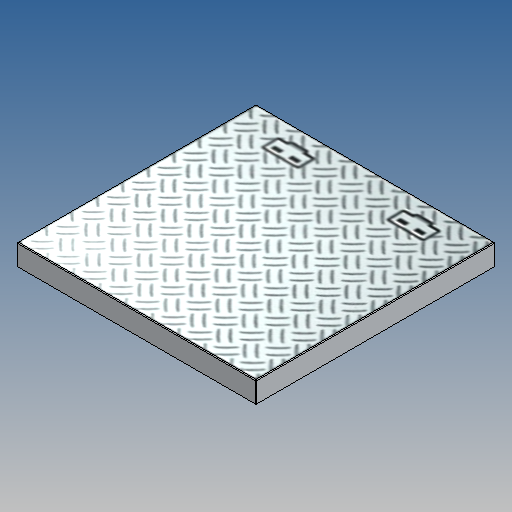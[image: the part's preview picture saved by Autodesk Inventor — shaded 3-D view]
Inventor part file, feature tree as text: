
AUTODESK INVENTOR PART (.ipt)
format: ipt  version: 2025 (Build 290162010, 162A)  size: 711,680 bytes
history: native  units: in
note: dims shown in document units (in); Inventor stores cm internally (conversion verified against a paired STEP export)
features: other x6, extrude x4, sketch x3, pattern_linear x1, fillet x1
ambient origin geometry x8: Origin, YZ Plane, XZ Plane, XY Plane, X Axis, Y Axis, Z Axis, Center Point
bodies: Solid1 (feature_tree)
feature tree (15):
  extrude  "Extrusion1"  Depth=1.2598in
  sketch  "Sketch3"  dims[d4=0.126in d5=0.0in d7=0.0591in d11=0.063in d12=0.0in]
  extrude  "Extrusion2"  Depth=0.063in TaperAngle=0.0deg
  extrude  "Extrusion7"  Depth=0.315in
  extrude  "Extrusion6"  Depth=0.315in
  pattern_linear  "Rectangular Pattern3"  Spacing1=0.6299in  [1 undecoded]
  fillet  "Fillet1"  Radius=0.126in
  other  "Work Axis1"
  other  "Work Axis2"
  other  "Work Axis3"
  other  "Work Axis4"
  other  "Aufkleber1"
  sketch  "Sketch2"  dims[d0=1.2598in d1=1.2598in]
  sketch  "Skizze10"  dims[d22=0.0039in d61=0.189in d75=0.315in d76=0.6299in d86=0.126in d87=0.0709in d88=0.0in d89=1.1811in d91=0.315in d92=0.315in d93=0.0in d94=0.0in d95=0.0in d96=0.0in d97=0.0in d98=0.9449in d99=0.9449in d100=0.0in d101=0.0in d102=0.0157in d103=0.0157in d104=0.0157in d105=0.0in d106=0.315in d107=1.1811in d109=0.315in d123=0.0197in]
  other  "Bild1"
note: 1 required parameter value undecoded (feature->parameter linkage not recoverable at this tier; creation-order binding heuristic only, values carry confidence <= 0.55)
